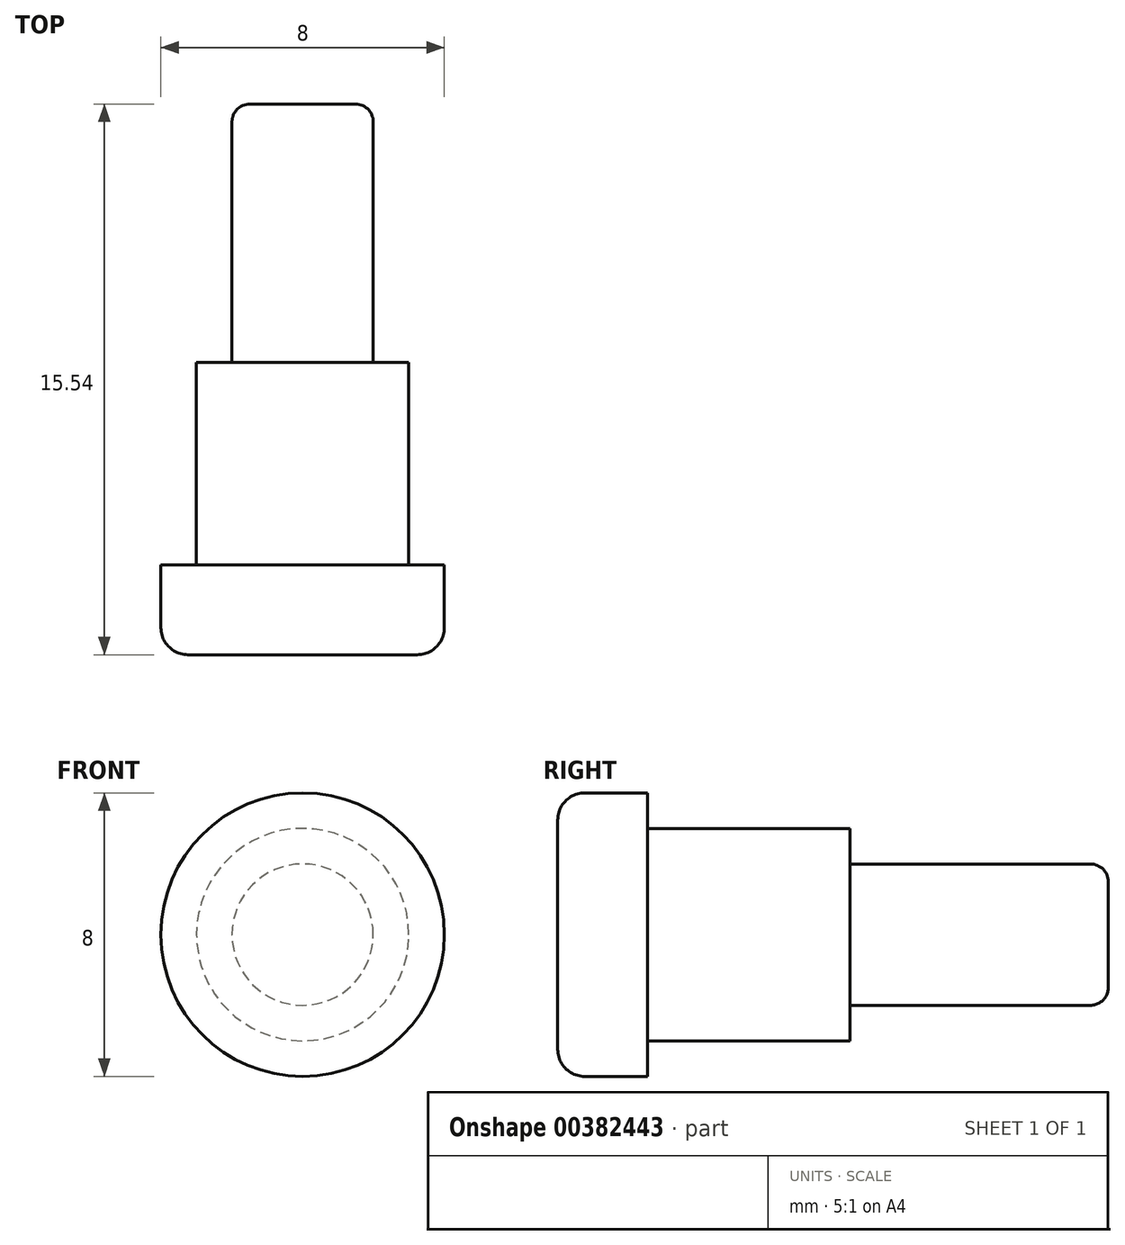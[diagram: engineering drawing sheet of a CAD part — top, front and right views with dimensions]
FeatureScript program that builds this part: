
annotation { "Feature Type Name" : "Feature", "Feature Type Description" : "" }
export const myFeature = defineFeature(function(context is Context, id is Id, definition is map)
    precondition{}
    {
        {
            var Q0;
            Q0=qCreatedBy(makeId("Front.planeOp"),FACE);
            var sketch = newSketch(context, id + "F0", { "sketchPlane" : qUnion([Q0])});
            skCircle(sketch, "E0", {"center": v(0, 0) * mm, "radius": 3 * mm});
            skCircle(sketch, "E1", {"center": v(0, 0) * mm, "radius": 4 * mm});
            skSolve(sketch);
        }
        {
            var Q0;
            Q0=makeQuery(id+"F0.imprint","IMPRINT",FACE,{"disambiguationData":[TD([[makeQuery(id+"F0.imprint","IMPRINT",EDGE,{"derivedFrom":sQuery(id+"F0.wireOp",EDGE,"E0")}),1.0]])]});
            extrude(context, id + "F1", {"entities" : qUnion([Q0]), "oppositeDirection" : true, "depth" : 8.25 * mm});
        }
        {
            var Q0;
            Q0=makeQuery(id+"F0.imprint","IMPRINT",FACE,{"disambiguationData":[TD([[makeQuery(id+"F0.imprint","IMPRINT",EDGE,{"derivedFrom":sQuery(id+"F0.wireOp",EDGE,"E0")}),-1.0]])]});
            extrude(context, id + "F2", {"entities" : qUnion([Q0]), "operationType" : NewBodyOperationType.ADD, "oppositeDirection" : true, "depth" : 2.54 * mm});
        }
        {
            var Q0;
            Q0=qCreatedBy(makeId("Front.planeOp"),FACE);
            var sketch = newSketch(context, id + "F3", { "sketchPlane" : qUnion([Q0])});
            skCircle(sketch, "E2", {"center": v(0, 0) * mm, "radius": 2 * mm});
            skSolve(sketch);
        }
        {
            var Q0;
            Q0 = qSketchRegion(id + "F3", true);
            extrude(context, id + "F4", {"entities" : qUnion([Q0]), "operationType" : NewBodyOperationType.ADD, "oppositeDirection" : true, "depth" : 15.54 * mm});
        }
        {
            var Q0;
            Q0=makeQuery(id+"F4.opExtrude","CAP_EDGE",EDGE,{"disambiguationData":[OSD([sQuery(id+"F3.wireOp",EDGE,"E2")])],"isStart":false});
            fillet(context, id + "F5", {"entities" : qUnion([Q0]), "radius" : 0.5 * mm, "allowEdgeOverflow" : false});
        }
        {
            var Q0;
            Q0=makeQuery(id+"F2.opExtrude","CAP_EDGE",EDGE,{"disambiguationData":[OSD([sQuery(id+"F0.wireOp",EDGE,"E1")])],"isStart":true});
            fillet(context, id + "F6", {"entities" : qUnion([Q0]), "radius" : 0.76 * mm, "tangentPropagation" : true, "allowEdgeOverflow" : false});
        }
    });
